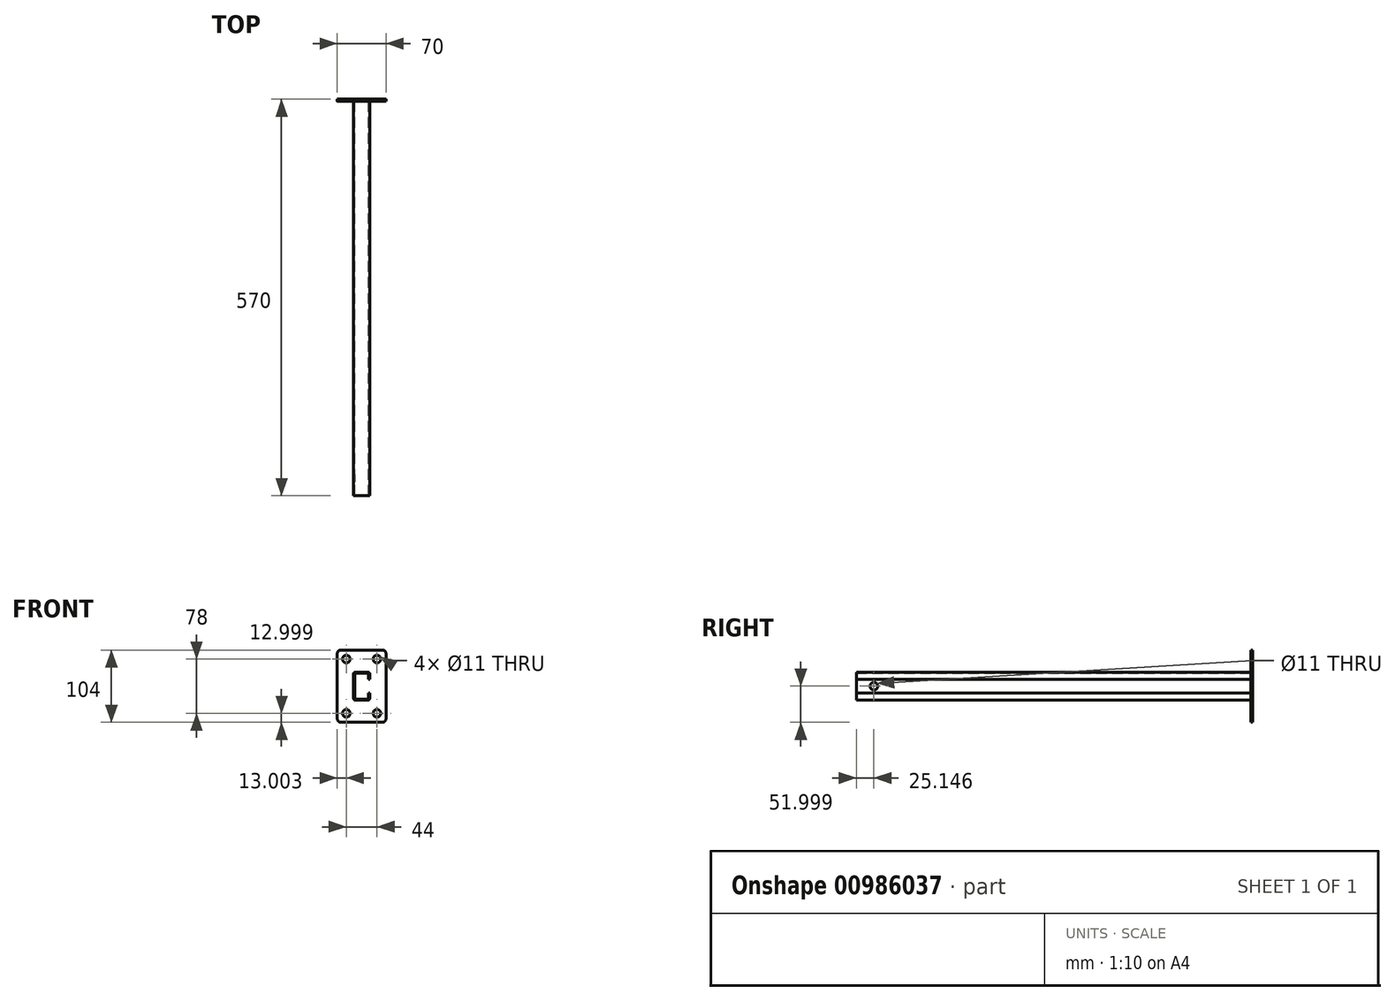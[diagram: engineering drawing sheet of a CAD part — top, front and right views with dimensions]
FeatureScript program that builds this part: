
annotation { "Feature Type Name" : "Feature", "Feature Type Description" : "" }
export const myFeature = defineFeature(function(context is Context, id is Id, definition is map)
    precondition{}
    {
        {
            var Q0;
            Q0=qCreatedBy(makeId("Front.planeOp"),FACE);
            var sketch = newSketch(context, id + "F0", { "sketchPlane" : qUnion([Q0])});
            skLineSegment(sketch, "E0.bottom", {"start": v(-106.84, 92.88) * mm, "end": v(-36.84, 92.88) * mm});
            skLineSegment(sketch, "E0.top", {"start": v(-106.84, -11.12) * mm, "end": v(-36.84, -11.12) * mm});
            skLineSegment(sketch, "E0.left", {"start": v(-106.84, 92.88) * mm, "end": v(-106.84, -11.12) * mm});
            skLineSegment(sketch, "E0.right", {"start": v(-36.84, 92.88) * mm, "end": v(-36.84, -11.12) * mm});
            skSolve(sketch);
        }
        {
            var Q0;
            Q0=makeQuery(id+"F0.imprint","IMPRINT",FACE,{"disambiguationData":[TD([[makeQuery(id+"F0.imprint","IMPRINT",EDGE,{"derivedFrom":sQuery(id+"F0.wireOp",EDGE,"E0.bottom")}),-1.0]])]});
            extrude(context, id + "F1", {"entities" : qUnion([Q0]), "depth" : 3 * mm, "offsetDistance" : 25 * mm});
        }
        {
            var Q0;
            Q0=makeQuery(id+"F1.opExtrude","SWEPT_EDGE",EDGE,{"disambiguationData":[OSD([sQuery(id+"F0.wireOp",EDGE,"E0.bottom"),sQuery(id+"F0.wireOp",EDGE,"E0.right")])]});
            var Q1;
            Q1=makeQuery(id+"F1.opExtrude","SWEPT_EDGE",EDGE,{"disambiguationData":[OSD([sQuery(id+"F0.wireOp",EDGE,"E0.bottom"),sQuery(id+"F0.wireOp",EDGE,"E0.left")])]});
            var Q2;
            Q2=makeQuery(id+"F1.opExtrude","SWEPT_EDGE",EDGE,{"disambiguationData":[OSD([sQuery(id+"F0.wireOp",EDGE,"E0.top"),sQuery(id+"F0.wireOp",EDGE,"E0.left")])]});
            var Q3;
            Q3=makeQuery(id+"F1.opExtrude","SWEPT_EDGE",EDGE,{"disambiguationData":[OSD([sQuery(id+"F0.wireOp",EDGE,"E0.top"),sQuery(id+"F0.wireOp",EDGE,"E0.right")])]});
            fillet(context, id + "F2", {"entities" : qUnion([Q0, Q1, Q2, Q3]), "radius" : 5 * mm, "tangentPropagation" : true, "allowEdgeOverflow" : false});
        }
        {
            var Q0;
            Q0=makeQuery(id+"F1.opExtrude","CAP_FACE",FACE,{"disambiguationData":[OSD([sQuery(id+"F0.wireOp",EDGE,"E0.bottom"),sQuery(id+"F0.wireOp",EDGE,"E0.top"),sQuery(id+"F0.wireOp",EDGE,"E0.left"),sQuery(id+"F0.wireOp",EDGE,"E0.right")])],"isStart":false});
            var sketch = newSketch(context, id + "F3", { "sketchPlane" : qUnion([Q0])});
            skCircle(sketch, "E1", {"center": v(-49.84, 1.88) * mm, "radius": 5.5 * mm});
            skCircle(sketch, "E2", {"center": v(-93.84, 1.88) * mm, "radius": 5.5 * mm});
            skCircle(sketch, "E3", {"center": v(-93.84, 79.88) * mm, "radius": 5.5 * mm});
            skCircle(sketch, "E4", {"center": v(-49.84, 79.88) * mm, "radius": 5.5 * mm});
            skSolve(sketch);
        }
        {
            var Q0;
            Q0=sQuery(id+"F3.wireOp",VERTEX,"E1.center");
            var Q1;
            Q1=sQuery(id+"F3.wireOp",VERTEX,"E2.center");
            var Q2;
            Q2=sQuery(id+"F3.wireOp",VERTEX,"E3.center");
            var Q3;
            Q3=sQuery(id+"F3.wireOp",VERTEX,"E4.center");
            var Q4;
            Q4=makeQuery(id+"F1.opExtrude","SWEPT_BODY",BODY,{"disambiguationData":[OSD([sQuery(id+"F0.wireOp",EDGE,"E0.bottom"),sQuery(id+"F0.wireOp",EDGE,"E0.top"),sQuery(id+"F0.wireOp",EDGE,"E0.left"),sQuery(id+"F0.wireOp",EDGE,"E0.right")])]});
            hole(context, id + "F4", {"style" : HoleStyle.SIMPLE, "endStyle" : HoleEndStyle.THROUGH, "holeDiameter" : 11 * mm, "majorDiameter" : 5 * mm, "isTappedThrough" : true, "tappedDepth" : 12 * mm, "tapClearance" : 3, "locations" : qUnion([Q0, Q1, Q2, Q3]), "scope" : qUnion([Q4])});
        }
        {
            var Q0;
            Q0=makeQuery(id+"F1.opExtrude","CAP_FACE",FACE,{"disambiguationData":[OSD([sQuery(id+"F0.wireOp",EDGE,"E0.bottom"),sQuery(id+"F0.wireOp",EDGE,"E0.top"),sQuery(id+"F0.wireOp",EDGE,"E0.left"),sQuery(id+"F0.wireOp",EDGE,"E0.right")])],"isStart":false});
            var sketch = newSketch(context, id + "F5", { "sketchPlane" : qUnion([Q0])});
            skPoint(sketch, "E5.visualSharp", {"position": v(-91.84, 27.27) * mm});
            skPoint(sketch, "E6.visualSharp", {"position": v(-90.34, 28.77) * mm});
            skLineSegment(sketch, "E7", {"start": v(-62.34, 60.88) * mm, "end": v(-81.34, 60.88) * mm});
            skLineSegment(sketch, "E8", {"start": v(-83.34, 58.88) * mm, "end": v(-83.34, 22.88) * mm});
            skLineSegment(sketch, "E9", {"start": v(-81.34, 20.88) * mm, "end": v(-62.34, 20.88) * mm});
            skLineSegment(sketch, "E10", {"start": v(-60.34, 22.88) * mm, "end": v(-60.34, 30.88) * mm});
            skLineSegment(sketch, "E11", {"start": v(-60.34, 30.88) * mm, "end": v(-61.84, 30.88) * mm});
            skLineSegment(sketch, "E12", {"start": v(-61.84, 30.88) * mm, "end": v(-61.84, 23.38) * mm});
            skLineSegment(sketch, "E13", {"start": v(-62.84, 22.38) * mm, "end": v(-80.84, 22.38) * mm});
            skLineSegment(sketch, "E14", {"start": v(-80.84, 59.38) * mm, "end": v(-62.84, 59.38) * mm});
            skLineSegment(sketch, "E15", {"start": v(-61.84, 58.38) * mm, "end": v(-61.84, 50.88) * mm});
            skLineSegment(sketch, "E16", {"start": v(-61.84, 50.88) * mm, "end": v(-60.34, 50.88) * mm});
            skLineSegment(sketch, "E17", {"start": v(-60.34, 58.88) * mm, "end": v(-60.34, 50.88) * mm});
            skLineSegment(sketch, "E18", {"start": v(-81.84, 58.38) * mm, "end": v(-81.84, 23.38) * mm});
            skPoint(sketch, "E19.visualSharp", {"position": v(-60.34, 60.88) * mm});
            skArc(sketch, "E19.filletArc", {"start": v(-60.34, 58.88) * mm, "mid": v(-60.92, 60.3) * mm, "end": v(-62.34, 60.88) * mm});
            skPoint(sketch, "E20.visualSharp", {"position": v(-60.34, 20.88) * mm});
            skArc(sketch, "E20.filletArc", {"start": v(-62.34, 20.88) * mm, "mid": v(-60.92, 21.46) * mm, "end": v(-60.34, 22.88) * mm});
            skPoint(sketch, "E21.visualSharp", {"position": v(-83.34, 20.88) * mm});
            skArc(sketch, "E21.filletArc", {"start": v(-83.34, 22.88) * mm, "mid": v(-82.75, 21.46) * mm, "end": v(-81.34, 20.88) * mm});
            skPoint(sketch, "E22.visualSharp", {"position": v(-83.34, 60.88) * mm});
            skArc(sketch, "E22.filletArc", {"start": v(-81.34, 60.88) * mm, "mid": v(-82.75, 60.3) * mm, "end": v(-83.34, 58.88) * mm});
            skPoint(sketch, "E23.visualSharp", {"position": v(-81.84, 59.38) * mm});
            skArc(sketch, "E23.filletArc", {"start": v(-80.84, 59.38) * mm, "mid": v(-81.54, 59.09) * mm, "end": v(-81.84, 58.38) * mm});
            skPoint(sketch, "E24.visualSharp", {"position": v(-61.84, 59.38) * mm});
            skArc(sketch, "E24.filletArc", {"start": v(-61.84, 58.38) * mm, "mid": v(-62.13, 59.09) * mm, "end": v(-62.84, 59.38) * mm});
            skPoint(sketch, "E25.visualSharp", {"position": v(-61.84, 22.38) * mm});
            skArc(sketch, "E25.filletArc", {"start": v(-62.84, 22.38) * mm, "mid": v(-62.13, 22.67) * mm, "end": v(-61.84, 23.38) * mm});
            skPoint(sketch, "E26.visualSharp", {"position": v(-81.84, 22.38) * mm});
            skArc(sketch, "E26.filletArc", {"start": v(-81.84, 23.38) * mm, "mid": v(-81.54, 22.67) * mm, "end": v(-80.84, 22.38) * mm});
            skSolve(sketch);
        }
        {
            var Q0;
            Q0=makeQuery(id+"F5.imprint","IMPRINT",FACE,{"disambiguationData":[TD([[makeQuery(id+"F5.imprint","IMPRINT",EDGE,{"derivedFrom":sQuery(id+"F5.wireOp",EDGE,"E7")}),1.0]])]});
            extrude(context, id + "F6", {"entities" : qUnion([Q0]), "operationType" : NewBodyOperationType.ADD, "depth" : 444 * mm, "offsetDistance" : 25 * mm});
        }
        {
            var Q0;
            Q0=makeQuery(id+"F6.opExtrude","CAP_FACE",FACE,{"disambiguationData":[OSD([sQuery(id+"F5.wireOp",EDGE,"E7"),sQuery(id+"F5.wireOp",EDGE,"E8"),sQuery(id+"F5.wireOp",EDGE,"E9"),sQuery(id+"F5.wireOp",EDGE,"E10"),sQuery(id+"F5.wireOp",EDGE,"E11"),sQuery(id+"F5.wireOp",EDGE,"E12"),sQuery(id+"F5.wireOp",EDGE,"E13"),sQuery(id+"F5.wireOp",EDGE,"E14"),sQuery(id+"F5.wireOp",EDGE,"E15"),sQuery(id+"F5.wireOp",EDGE,"E16"),sQuery(id+"F5.wireOp",EDGE,"E17"),sQuery(id+"F5.wireOp",EDGE,"E18"),sQuery(id+"F5.wireOp",EDGE,"E19.filletArc"),sQuery(id+"F5.wireOp",EDGE,"E20.filletArc"),sQuery(id+"F5.wireOp",EDGE,"E21.filletArc"),sQuery(id+"F5.wireOp",EDGE,"E22.filletArc"),sQuery(id+"F5.wireOp",EDGE,"E23.filletArc"),sQuery(id+"F5.wireOp",EDGE,"E24.filletArc"),sQuery(id+"F5.wireOp",EDGE,"E25.filletArc"),sQuery(id+"F5.wireOp",EDGE,"E26.filletArc")])],"isStart":false});
            var sketch = newSketch(context, id + "F7", { "sketchPlane" : qUnion([Q0])});
            skLineSegment(sketch, "E27", {"start": v(-36.84, 92.88) * mm, "end": v(-36.84, -10.12) * mm});
            skLineSegment(sketch, "E28", {"start": v(-36.84, -10.12) * mm, "end": v(-106.84, -10.12) * mm});
            skLineSegment(sketch, "E29", {"start": v(-106.84, -10.12) * mm, "end": v(-106.84, 92.88) * mm});
            skLineSegment(sketch, "E30", {"start": v(-106.84, 92.88) * mm, "end": v(-36.84, 92.88) * mm});
            skSolve(sketch);
        }
        {
            var Q0;
            Q0=makeQuery(id+"F6.opExtrude","SWEPT_FACE",FACE,{"disambiguationData":[OSD([sQuery(id+"F5.wireOp",EDGE,"E8")])]});
            var sketch = newSketch(context, id + "F8", { "sketchPlane" : qUnion([Q0])});
            skCircle(sketch, "E31", {"center": v(544.85, 40.88) * mm, "radius": 5.5 * mm});
            skSolve(sketch);
        }
        {
            var Q0;
            Q0=makeQuery(id+"F7.imprint","IMPRINT",FACE,{"disambiguationData":[TD([[makeQuery(id+"F7.imprint","IMPRINT",EDGE,{"derivedFrom":makeQuery(id+"F6.opExtrude","CAP_EDGE",EDGE,{"disambiguationData":[OSD([sQuery(id+"F5.wireOp",EDGE,"E7")])],"isStart":false})}),1.0]])]});
            extrude(context, id + "F9", {"entities" : qUnion([Q0]), "operationType" : NewBodyOperationType.ADD, "depth" : 123 * mm, "offsetDistance" : 25 * mm});
        }
        {
            var Q0;
            Q0=sQuery(id+"F8.wireOp",VERTEX,"E31.center");
            var Q1;
            Q1=makeQuery(id+"F1.opExtrude","SWEPT_BODY",BODY,{"disambiguationData":[OSD([sQuery(id+"F0.wireOp",EDGE,"E0.bottom"),sQuery(id+"F0.wireOp",EDGE,"E0.top"),sQuery(id+"F0.wireOp",EDGE,"E0.left"),sQuery(id+"F0.wireOp",EDGE,"E0.right")])]});
            hole(context, id + "F10", {"style" : HoleStyle.SIMPLE, "endStyle" : HoleEndStyle.THROUGH, "holeDiameter" : 11 * mm, "majorDiameter" : 5 * mm, "isTappedThrough" : true, "tappedDepth" : 12 * mm, "tapClearance" : 3, "locations" : qUnion([Q0]), "scope" : qUnion([Q1])});
        }
    });
